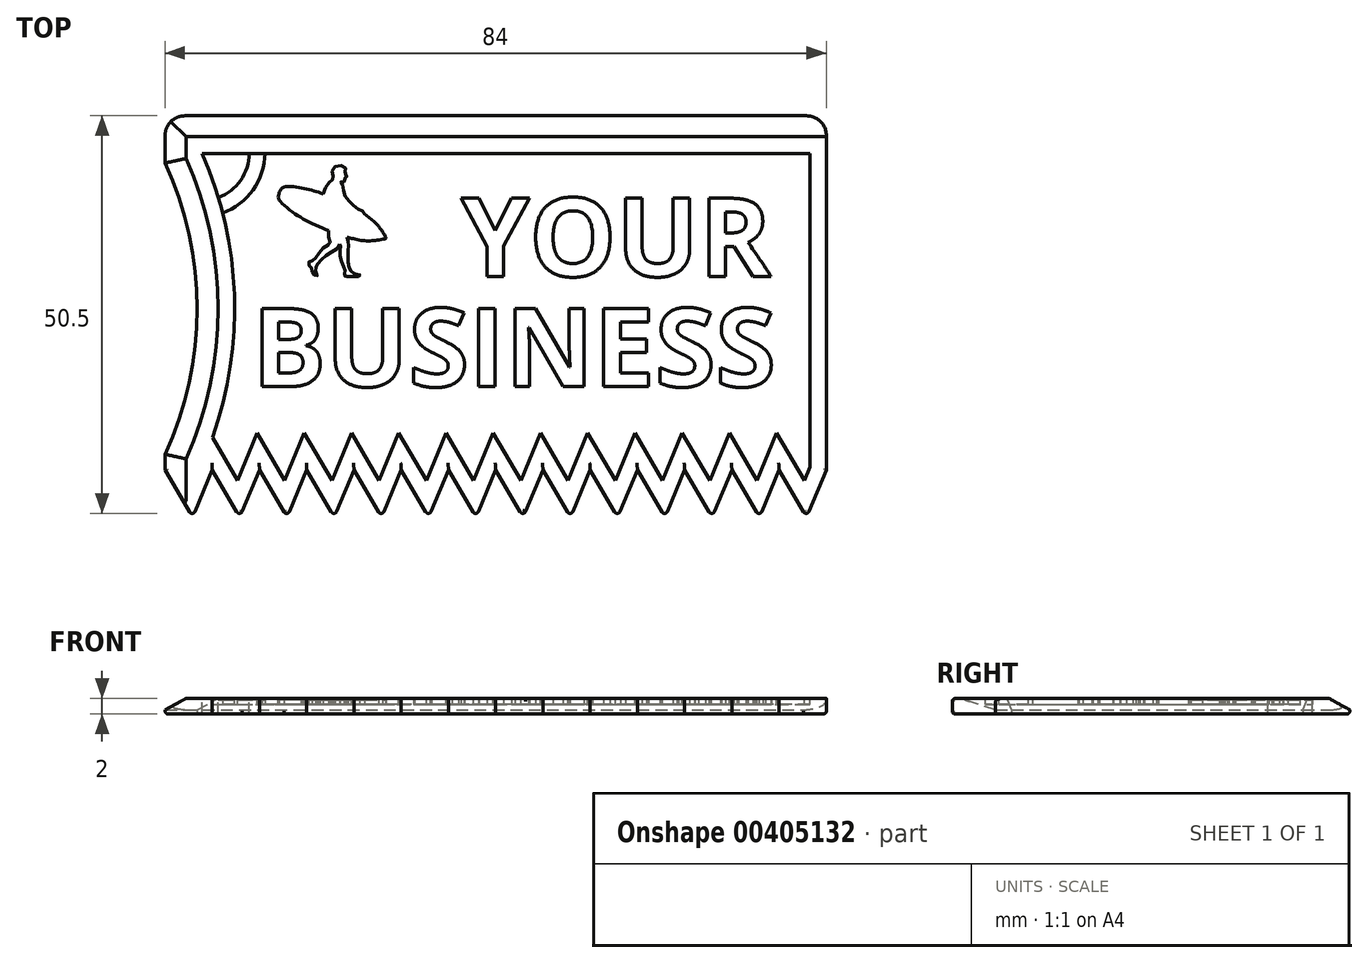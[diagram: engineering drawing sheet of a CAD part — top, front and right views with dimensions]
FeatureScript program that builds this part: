
annotation { "Feature Type Name" : "Feature", "Feature Type Description" : "" }
export const myFeature = defineFeature(function(context is Context, id is Id, definition is map)
    precondition{}
    {
        {
            assignVariable(context, id + "F0", {"name" : "t", "anyValue" : 2});
        }
        {
            var Q0;
            Q0=qCreatedBy(makeId("Top.planeOp"),FACE);
            var sketch = newSketch(context, id + "F1", { "sketchPlane" : qUnion([Q0])});
            skLineSegment(sketch, "E0.bottom", {"start": v(84, 51) * mm, "end": v(0, 51) * mm});
            skLineSegment(sketch, "E0.top", {"start": v(81.5, 0) * mm, "end": v(3.5, 0) * mm, "construction": true});
            skLineSegment(sketch, "E0.left", {"start": v(84, 51) * mm, "end": v(84, 6) * mm});
            skLineSegment(sketch, "E0.right", {"start": v(0, 51) * mm, "end": v(0, 6) * mm, "construction": true});
            skLineSegment(sketch, "E1", {"start": v(84, 6) * mm, "end": v(0, 6) * mm, "construction": true});
            skLineSegment(sketch, "E2", {"start": v(84, 6) * mm, "end": v(81.5, 0) * mm});
            skLineSegment(sketch, "E3", {"start": v(81.5, 0) * mm, "end": v(78, 6) * mm});
            skLineSegment(sketch, "E4.1.0.0", {"start": v(78, 6) * mm, "end": v(75.5, 0) * mm});
            skLineSegment(sketch, "E4.1.0.1", {"start": v(75.5, 0) * mm, "end": v(72, 6) * mm});
            skLineSegment(sketch, "E4.2.0.0", {"start": v(72, 6) * mm, "end": v(69.5, 0) * mm});
            skLineSegment(sketch, "E4.2.0.1", {"start": v(69.5, 0) * mm, "end": v(66, 6) * mm});
            skLineSegment(sketch, "E4.3.0.0", {"start": v(66, 6) * mm, "end": v(63.5, 0) * mm});
            skLineSegment(sketch, "E4.3.0.1", {"start": v(63.5, 0) * mm, "end": v(60, 6) * mm});
            skLineSegment(sketch, "E4.4.0.0", {"start": v(60, 6) * mm, "end": v(57.5, 0) * mm});
            skLineSegment(sketch, "E4.4.0.1", {"start": v(57.5, 0) * mm, "end": v(54, 6) * mm});
            skLineSegment(sketch, "E4.5.0.0", {"start": v(54, 6) * mm, "end": v(51.5, 0) * mm});
            skLineSegment(sketch, "E4.5.0.1", {"start": v(51.5, 0) * mm, "end": v(48, 6) * mm});
            skLineSegment(sketch, "E4.6.0.0", {"start": v(48, 6) * mm, "end": v(45.5, 0) * mm});
            skLineSegment(sketch, "E4.6.0.1", {"start": v(45.5, 0) * mm, "end": v(42, 6) * mm});
            skLineSegment(sketch, "E4.7.0.0", {"start": v(42, 6) * mm, "end": v(39.5, 0) * mm});
            skLineSegment(sketch, "E4.7.0.1", {"start": v(39.5, 0) * mm, "end": v(36, 6) * mm});
            skLineSegment(sketch, "E4.8.0.0", {"start": v(36, 6) * mm, "end": v(33.5, 0) * mm});
            skLineSegment(sketch, "E4.8.0.1", {"start": v(33.5, 0) * mm, "end": v(30, 6) * mm});
            skLineSegment(sketch, "E4.9.0.0", {"start": v(30, 6) * mm, "end": v(27.5, 0) * mm});
            skLineSegment(sketch, "E4.9.0.1", {"start": v(27.5, 0) * mm, "end": v(24, 6) * mm});
            skLineSegment(sketch, "E4.10.0.0", {"start": v(24, 6) * mm, "end": v(21.5, 0) * mm});
            skLineSegment(sketch, "E4.10.0.1", {"start": v(21.5, 0) * mm, "end": v(18, 6) * mm});
            skLineSegment(sketch, "E4.11.0.0", {"start": v(18, 6) * mm, "end": v(15.5, 0) * mm});
            skLineSegment(sketch, "E4.11.0.1", {"start": v(15.5, 0) * mm, "end": v(12, 6) * mm});
            skLineSegment(sketch, "E4.12.0.0", {"start": v(12, 6) * mm, "end": v(9.5, 0) * mm});
            skLineSegment(sketch, "E4.12.0.1", {"start": v(9.5, 0) * mm, "end": v(6, 6) * mm});
            skLineSegment(sketch, "E4.13.0.0", {"start": v(6, 6) * mm, "end": v(3.5, 0) * mm});
            skLineSegment(sketch, "E4.13.0.1", {"start": v(3.5, 0) * mm, "end": v(0, 6) * mm});
            skLineSegment(sketch, "E4.direction1", {"start": v(84, 6) * mm, "end": v(78, 6) * mm, "construction": true});
            skLineSegment(sketch, "E5", {"start": v(0, 6) * mm, "end": v(0, 8) * mm});
            skArc(sketch, "E6", {"start": v(0, 8) * mm, "mid": v(4.07, 26.5) * mm, "end": v(0, 45) * mm});
            skLineSegment(sketch, "E7", {"start": v(0, 45) * mm, "end": v(0, 51) * mm});
            skLineSegment(sketch, "E8", {"start": v(0, 6) * mm, "end": v(0, 0) * mm, "construction": true});
            skSolve(sketch);
        }
        {
            var Q0;
            Q0=qSketchRegion(id+"F1",true);
            extrude(context, id + "F2", {"entities" : qUnion([Q0]), "depth" : (getVariable(context, 't')) * mm});
        }
        {
            var Q0;
            Q0=makeQuery(id+"F2.opExtrude","CAP_EDGE",EDGE,{"disambiguationData":[OSD([sQuery(id+"F1.wireOp",EDGE,"E5")])],"isStart":false});
            var Q1;
            Q1=makeQuery(id+"F2.opExtrude","CAP_EDGE",EDGE,{"disambiguationData":[OSD([sQuery(id+"F1.wireOp",EDGE,"E6")])],"isStart":false});
            var Q2;
            Q2=makeQuery(id+"F2.opExtrude","CAP_EDGE",EDGE,{"disambiguationData":[OSD([sQuery(id+"F1.wireOp",EDGE,"E0.bottom")])],"isStart":false});
            var Q3;
            Q3=makeQuery(id+"F2.opExtrude","CAP_EDGE",EDGE,{"disambiguationData":[OSD([sQuery(id+"F1.wireOp",EDGE,"E7")])],"isStart":false});
            chamfer(context, id + "F3", {"entities" : qUnion([Q0, Q1, Q2, Q3]), "chamferType" : ChamferType.TWO_OFFSETS, "width1" : (getVariable(context, 't') * 2.2 / 3) * mm, "oppositeDirection" : false, "width2" : (getVariable(context, 't') * 4 / 3) * mm, "tangentPropagation" : true});
        }
        {
            var Q0;
            Q0=makeQuery(id+"F2.opExtrude","SWEPT_EDGE",EDGE,{"disambiguationData":[OSD([sQuery(id+"F1.wireOp",EDGE,"E0.bottom"),sQuery(id+"F1.wireOp",EDGE,"E7")])]});
            var Q1;
            Q1=makeQuery(id+"F2.opExtrude","SWEPT_EDGE",EDGE,{"disambiguationData":[OSD([sQuery(id+"F1.wireOp",EDGE,"E0.bottom"),sQuery(id+"F1.wireOp",EDGE,"E0.left")])]});
            fillet(context, id + "F4", {"entities" : qUnion([Q0, Q1]), "radius" : 2.5 * mm, "tangentPropagation" : true, "allowEdgeOverflow" : false});
        }
        {
            var Q0;
            Q0=makeQuery(id+"F2.opExtrude","CAP_FACE",FACE,{"disambiguationData":[OSD([sQuery(id+"F1.wireOp",EDGE,"E0.bottom"),sQuery(id+"F1.wireOp",EDGE,"E0.left"),sQuery(id+"F1.wireOp",EDGE,"E2"),sQuery(id+"F1.wireOp",EDGE,"E3"),sQuery(id+"F1.wireOp",EDGE,"E4.1.0.0"),sQuery(id+"F1.wireOp",EDGE,"E4.1.0.1"),sQuery(id+"F1.wireOp",EDGE,"E4.2.0.0"),sQuery(id+"F1.wireOp",EDGE,"E4.2.0.1"),sQuery(id+"F1.wireOp",EDGE,"E4.3.0.0"),sQuery(id+"F1.wireOp",EDGE,"E4.3.0.1"),sQuery(id+"F1.wireOp",EDGE,"E4.4.0.0"),sQuery(id+"F1.wireOp",EDGE,"E4.4.0.1"),sQuery(id+"F1.wireOp",EDGE,"E4.5.0.0"),sQuery(id+"F1.wireOp",EDGE,"E4.5.0.1"),sQuery(id+"F1.wireOp",EDGE,"E4.6.0.0"),sQuery(id+"F1.wireOp",EDGE,"E4.6.0.1"),sQuery(id+"F1.wireOp",EDGE,"E4.7.0.0"),sQuery(id+"F1.wireOp",EDGE,"E4.7.0.1"),sQuery(id+"F1.wireOp",EDGE,"E4.8.0.0"),sQuery(id+"F1.wireOp",EDGE,"E4.8.0.1"),sQuery(id+"F1.wireOp",EDGE,"E4.9.0.0"),sQuery(id+"F1.wireOp",EDGE,"E4.9.0.1"),sQuery(id+"F1.wireOp",EDGE,"E4.10.0.0"),sQuery(id+"F1.wireOp",EDGE,"E4.10.0.1"),sQuery(id+"F1.wireOp",EDGE,"E4.11.0.0"),sQuery(id+"F1.wireOp",EDGE,"E4.11.0.1"),sQuery(id+"F1.wireOp",EDGE,"E4.12.0.0"),sQuery(id+"F1.wireOp",EDGE,"E4.12.0.1"),sQuery(id+"F1.wireOp",EDGE,"E4.13.0.0"),sQuery(id+"F1.wireOp",EDGE,"E4.13.0.1"),sQuery(id+"F1.wireOp",EDGE,"E5"),sQuery(id+"F1.wireOp",EDGE,"E6"),sQuery(id+"F1.wireOp",EDGE,"E7")])],"isStart":false});
            var sketch = newSketch(context, id + "F5", { "sketchPlane" : qUnion([Q0])});
            skLineSegment(sketch, "E9.0", {"start": v(81.9, 6.42) * mm, "end": v(81.9, 46.23) * mm});
            skLineSegment(sketch, "E9.1", {"start": v(81.19, 4.7) * mm, "end": v(81.9, 6.42) * mm});
            skLineSegment(sketch, "E9.2", {"start": v(77.69, 10.7) * mm, "end": v(81.19, 4.7) * mm});
            skLineSegment(sketch, "E9.3", {"start": v(75.19, 4.7) * mm, "end": v(77.69, 10.7) * mm});
            skLineSegment(sketch, "E9.4", {"start": v(71.69, 10.7) * mm, "end": v(75.19, 4.7) * mm});
            skLineSegment(sketch, "E9.5", {"start": v(69.19, 4.7) * mm, "end": v(71.69, 10.7) * mm});
            skLineSegment(sketch, "E9.6", {"start": v(65.69, 10.7) * mm, "end": v(69.19, 4.7) * mm});
            skLineSegment(sketch, "E9.7", {"start": v(81.9, 46.23) * mm, "end": v(4.67, 46.23) * mm});
            skArc(sketch, "E9.8", {"start": v(4.67, 46.23) * mm, "mid": v(8.8, 28.32) * mm, "end": v(6.02, 10.14) * mm});
            skLineSegment(sketch, "E9.9", {"start": v(6.02, 10.14) * mm, "end": v(9.19, 4.7) * mm});
            skLineSegment(sketch, "E9.10", {"start": v(9.19, 4.7) * mm, "end": v(11.69, 10.7) * mm});
            skLineSegment(sketch, "E9.11", {"start": v(11.69, 10.7) * mm, "end": v(15.19, 4.7) * mm});
            skLineSegment(sketch, "E9.12", {"start": v(15.19, 4.7) * mm, "end": v(17.69, 10.7) * mm});
            skLineSegment(sketch, "E9.13", {"start": v(17.69, 10.7) * mm, "end": v(21.19, 4.7) * mm});
            skLineSegment(sketch, "E9.14", {"start": v(21.19, 4.7) * mm, "end": v(23.69, 10.7) * mm});
            skLineSegment(sketch, "E9.15", {"start": v(23.69, 10.7) * mm, "end": v(27.19, 4.7) * mm});
            skLineSegment(sketch, "E9.16", {"start": v(27.19, 4.7) * mm, "end": v(29.69, 10.7) * mm});
            skLineSegment(sketch, "E9.17", {"start": v(29.69, 10.7) * mm, "end": v(33.19, 4.7) * mm});
            skLineSegment(sketch, "E9.18", {"start": v(33.19, 4.7) * mm, "end": v(35.69, 10.7) * mm});
            skLineSegment(sketch, "E9.19", {"start": v(35.69, 10.7) * mm, "end": v(39.19, 4.7) * mm});
            skLineSegment(sketch, "E9.20", {"start": v(39.19, 4.7) * mm, "end": v(41.69, 10.7) * mm});
            skLineSegment(sketch, "E9.21", {"start": v(41.69, 10.7) * mm, "end": v(45.19, 4.7) * mm});
            skLineSegment(sketch, "E9.22", {"start": v(45.19, 4.7) * mm, "end": v(47.69, 10.7) * mm});
            skLineSegment(sketch, "E9.23", {"start": v(47.69, 10.7) * mm, "end": v(51.19, 4.7) * mm});
            skLineSegment(sketch, "E9.24", {"start": v(51.19, 4.7) * mm, "end": v(53.69, 10.7) * mm});
            skLineSegment(sketch, "E9.25", {"start": v(53.69, 10.7) * mm, "end": v(57.19, 4.7) * mm});
            skLineSegment(sketch, "E9.26", {"start": v(57.19, 4.7) * mm, "end": v(59.69, 10.7) * mm});
            skLineSegment(sketch, "E9.27", {"start": v(59.69, 10.7) * mm, "end": v(63.19, 4.7) * mm});
            skLineSegment(sketch, "E9.28", {"start": v(63.19, 4.7) * mm, "end": v(65.69, 10.7) * mm});
            skSolve(sketch);
        }
        {
            var Q0;
            Q0=makeQuery(id+"F5.imprint","IMPRINT",FACE,{"disambiguationData":[TD([[makeQuery(id+"F5.imprint","IMPRINT",EDGE,{"derivedFrom":sQuery(id+"F5.wireOp",EDGE,"E9.0")}),1.0]])]});
            extrude(context, id + "F6", {"entities" : qUnion([Q0]), "operationType" : NewBodyOperationType.REMOVE, "oppositeDirection" : true, "depth" : (getVariable(context, 't') * 2 / 5) * mm});
        }
        {
            var Q0;
            Q0=makeQuery(id+"F2.opExtrude","CAP_FACE",FACE,{"disambiguationData":[OSD([sQuery(id+"F1.wireOp",EDGE,"E0.bottom"),sQuery(id+"F1.wireOp",EDGE,"E0.left"),sQuery(id+"F1.wireOp",EDGE,"E2"),sQuery(id+"F1.wireOp",EDGE,"E3"),sQuery(id+"F1.wireOp",EDGE,"E4.1.0.0"),sQuery(id+"F1.wireOp",EDGE,"E4.1.0.1"),sQuery(id+"F1.wireOp",EDGE,"E4.2.0.0"),sQuery(id+"F1.wireOp",EDGE,"E4.2.0.1"),sQuery(id+"F1.wireOp",EDGE,"E4.3.0.0"),sQuery(id+"F1.wireOp",EDGE,"E4.3.0.1"),sQuery(id+"F1.wireOp",EDGE,"E4.4.0.0"),sQuery(id+"F1.wireOp",EDGE,"E4.4.0.1"),sQuery(id+"F1.wireOp",EDGE,"E4.5.0.0"),sQuery(id+"F1.wireOp",EDGE,"E4.5.0.1"),sQuery(id+"F1.wireOp",EDGE,"E4.6.0.0"),sQuery(id+"F1.wireOp",EDGE,"E4.6.0.1"),sQuery(id+"F1.wireOp",EDGE,"E4.7.0.0"),sQuery(id+"F1.wireOp",EDGE,"E4.7.0.1"),sQuery(id+"F1.wireOp",EDGE,"E4.8.0.0"),sQuery(id+"F1.wireOp",EDGE,"E4.8.0.1"),sQuery(id+"F1.wireOp",EDGE,"E4.9.0.0"),sQuery(id+"F1.wireOp",EDGE,"E4.9.0.1"),sQuery(id+"F1.wireOp",EDGE,"E4.10.0.0"),sQuery(id+"F1.wireOp",EDGE,"E4.10.0.1"),sQuery(id+"F1.wireOp",EDGE,"E4.11.0.0"),sQuery(id+"F1.wireOp",EDGE,"E4.11.0.1"),sQuery(id+"F1.wireOp",EDGE,"E4.12.0.0"),sQuery(id+"F1.wireOp",EDGE,"E4.12.0.1"),sQuery(id+"F1.wireOp",EDGE,"E4.13.0.0"),sQuery(id+"F1.wireOp",EDGE,"E4.13.0.1"),sQuery(id+"F1.wireOp",EDGE,"E5"),sQuery(id+"F1.wireOp",EDGE,"E6"),sQuery(id+"F1.wireOp",EDGE,"E7")])],"isStart":true});
            var Q1;
            Q1=makeQuery(id+"F2.opExtrude","CAP_EDGE",EDGE,{"disambiguationData":[OSD([sQuery(id+"F1.wireOp",EDGE,"E4.13.0.1")])],"isStart":false});
            var Q2;
            Q2=makeQuery(id+"F2.opExtrude","CAP_EDGE",EDGE,{"disambiguationData":[OSD([sQuery(id+"F1.wireOp",EDGE,"E4.13.0.0")])],"isStart":false});
            var Q3;
            Q3=makeQuery(id+"F2.opExtrude","SWEPT_EDGE",EDGE,{"disambiguationData":[OSD([sQuery(id+"F1.wireOp",EDGE,"E4.13.0.0"),sQuery(id+"F1.wireOp",EDGE,"E4.13.0.1")])]});
            var Q4;
            Q4=makeQuery(id+"F2.opExtrude","CAP_EDGE",EDGE,{"disambiguationData":[OSD([sQuery(id+"F1.wireOp",EDGE,"E4.12.0.1")])],"isStart":false});
            var Q5;
            Q5=makeQuery(id+"F2.opExtrude","SWEPT_EDGE",EDGE,{"disambiguationData":[OSD([sQuery(id+"F1.wireOp",EDGE,"E4.12.0.0"),sQuery(id+"F1.wireOp",EDGE,"E4.12.0.1")])]});
            var Q6;
            Q6=makeQuery(id+"F2.opExtrude","CAP_EDGE",EDGE,{"disambiguationData":[OSD([sQuery(id+"F1.wireOp",EDGE,"E4.12.0.0")])],"isStart":false});
            var Q7;
            Q7=makeQuery(id+"F2.opExtrude","CAP_EDGE",EDGE,{"disambiguationData":[OSD([sQuery(id+"F1.wireOp",EDGE,"E4.11.0.1")])],"isStart":false});
            var Q8;
            Q8=makeQuery(id+"F2.opExtrude","SWEPT_EDGE",EDGE,{"disambiguationData":[OSD([sQuery(id+"F1.wireOp",EDGE,"E4.11.0.0"),sQuery(id+"F1.wireOp",EDGE,"E4.11.0.1")])]});
            var Q9;
            Q9=makeQuery(id+"F2.opExtrude","CAP_EDGE",EDGE,{"disambiguationData":[OSD([sQuery(id+"F1.wireOp",EDGE,"E4.11.0.0")])],"isStart":false});
            var Q10;
            Q10=makeQuery(id+"F2.opExtrude","CAP_EDGE",EDGE,{"disambiguationData":[OSD([sQuery(id+"F1.wireOp",EDGE,"E4.10.0.1")])],"isStart":false});
            var Q11;
            Q11=makeQuery(id+"F2.opExtrude","CAP_EDGE",EDGE,{"disambiguationData":[OSD([sQuery(id+"F1.wireOp",EDGE,"E4.10.0.0")])],"isStart":false});
            var Q12;
            Q12=makeQuery(id+"F2.opExtrude","CAP_EDGE",EDGE,{"disambiguationData":[OSD([sQuery(id+"F1.wireOp",EDGE,"E4.9.0.1")])],"isStart":false});
            var Q13;
            Q13=makeQuery(id+"F2.opExtrude","CAP_EDGE",EDGE,{"disambiguationData":[OSD([sQuery(id+"F1.wireOp",EDGE,"E4.9.0.0")])],"isStart":false});
            var Q14;
            Q14=makeQuery(id+"F2.opExtrude","CAP_EDGE",EDGE,{"disambiguationData":[OSD([sQuery(id+"F1.wireOp",EDGE,"E4.8.0.1")])],"isStart":false});
            var Q15;
            Q15=makeQuery(id+"F2.opExtrude","CAP_EDGE",EDGE,{"disambiguationData":[OSD([sQuery(id+"F1.wireOp",EDGE,"E4.8.0.0")])],"isStart":false});
            var Q16;
            Q16=makeQuery(id+"F2.opExtrude","CAP_EDGE",EDGE,{"disambiguationData":[OSD([sQuery(id+"F1.wireOp",EDGE,"E4.7.0.1")])],"isStart":false});
            var Q17;
            Q17=makeQuery(id+"F2.opExtrude","CAP_EDGE",EDGE,{"disambiguationData":[OSD([sQuery(id+"F1.wireOp",EDGE,"E4.7.0.0")])],"isStart":false});
            var Q18;
            Q18=makeQuery(id+"F2.opExtrude","CAP_EDGE",EDGE,{"disambiguationData":[OSD([sQuery(id+"F1.wireOp",EDGE,"E4.6.0.1")])],"isStart":false});
            var Q19;
            Q19=makeQuery(id+"F2.opExtrude","CAP_EDGE",EDGE,{"disambiguationData":[OSD([sQuery(id+"F1.wireOp",EDGE,"E4.6.0.0")])],"isStart":false});
            var Q20;
            Q20=makeQuery(id+"F2.opExtrude","CAP_EDGE",EDGE,{"disambiguationData":[OSD([sQuery(id+"F1.wireOp",EDGE,"E4.5.0.1")])],"isStart":false});
            var Q21;
            Q21=makeQuery(id+"F2.opExtrude","CAP_EDGE",EDGE,{"disambiguationData":[OSD([sQuery(id+"F1.wireOp",EDGE,"E4.5.0.0")])],"isStart":false});
            var Q22;
            Q22=makeQuery(id+"F2.opExtrude","CAP_EDGE",EDGE,{"disambiguationData":[OSD([sQuery(id+"F1.wireOp",EDGE,"E4.4.0.1")])],"isStart":false});
            var Q23;
            Q23=makeQuery(id+"F2.opExtrude","CAP_EDGE",EDGE,{"disambiguationData":[OSD([sQuery(id+"F1.wireOp",EDGE,"E4.4.0.0")])],"isStart":false});
            var Q24;
            Q24=makeQuery(id+"F2.opExtrude","CAP_EDGE",EDGE,{"disambiguationData":[OSD([sQuery(id+"F1.wireOp",EDGE,"E4.3.0.1")])],"isStart":false});
            var Q25;
            Q25=makeQuery(id+"F2.opExtrude","CAP_EDGE",EDGE,{"disambiguationData":[OSD([sQuery(id+"F1.wireOp",EDGE,"E4.3.0.0")])],"isStart":false});
            var Q26;
            Q26=makeQuery(id+"F2.opExtrude","CAP_EDGE",EDGE,{"disambiguationData":[OSD([sQuery(id+"F1.wireOp",EDGE,"E4.2.0.1")])],"isStart":false});
            var Q27;
            Q27=makeQuery(id+"F2.opExtrude","CAP_EDGE",EDGE,{"disambiguationData":[OSD([sQuery(id+"F1.wireOp",EDGE,"E4.2.0.0")])],"isStart":false});
            var Q28;
            Q28=makeQuery(id+"F2.opExtrude","CAP_EDGE",EDGE,{"disambiguationData":[OSD([sQuery(id+"F1.wireOp",EDGE,"E4.1.0.1")])],"isStart":false});
            var Q29;
            Q29=makeQuery(id+"F2.opExtrude","CAP_EDGE",EDGE,{"disambiguationData":[OSD([sQuery(id+"F1.wireOp",EDGE,"E4.1.0.0")])],"isStart":false});
            var Q30;
            Q30=makeQuery(id+"F2.opExtrude","CAP_EDGE",EDGE,{"disambiguationData":[OSD([sQuery(id+"F1.wireOp",EDGE,"E3")])],"isStart":false});
            var Q31;
            Q31=makeQuery(id+"F2.opExtrude","SWEPT_EDGE",EDGE,{"disambiguationData":[OSD([sQuery(id+"F1.wireOp",EDGE,"E2"),sQuery(id+"F1.wireOp",EDGE,"E3")])]});
            var Q32;
            Q32=makeQuery(id+"F2.opExtrude","CAP_EDGE",EDGE,{"disambiguationData":[OSD([sQuery(id+"F1.wireOp",EDGE,"E2")])],"isStart":false});
            var Q33;
            Q33=makeQuery(id+"F2.opExtrude","SWEPT_EDGE",EDGE,{"disambiguationData":[OSD([sQuery(id+"F1.wireOp",EDGE,"E4.1.0.0"),sQuery(id+"F1.wireOp",EDGE,"E4.1.0.1")])]});
            var Q34;
            Q34=makeQuery(id+"F2.opExtrude","SWEPT_EDGE",EDGE,{"disambiguationData":[OSD([sQuery(id+"F1.wireOp",EDGE,"E4.2.0.0"),sQuery(id+"F1.wireOp",EDGE,"E4.2.0.1")])]});
            var Q35;
            Q35=makeQuery(id+"F2.opExtrude","SWEPT_EDGE",EDGE,{"disambiguationData":[OSD([sQuery(id+"F1.wireOp",EDGE,"E4.3.0.0"),sQuery(id+"F1.wireOp",EDGE,"E4.3.0.1")])]});
            var Q36;
            Q36=makeQuery(id+"F2.opExtrude","SWEPT_EDGE",EDGE,{"disambiguationData":[OSD([sQuery(id+"F1.wireOp",EDGE,"E4.4.0.0"),sQuery(id+"F1.wireOp",EDGE,"E4.4.0.1")])]});
            var Q37;
            Q37=makeQuery(id+"F2.opExtrude","SWEPT_EDGE",EDGE,{"disambiguationData":[OSD([sQuery(id+"F1.wireOp",EDGE,"E4.5.0.0"),sQuery(id+"F1.wireOp",EDGE,"E4.5.0.1")])]});
            var Q38;
            Q38=makeQuery(id+"F2.opExtrude","SWEPT_EDGE",EDGE,{"disambiguationData":[OSD([sQuery(id+"F1.wireOp",EDGE,"E4.6.0.0"),sQuery(id+"F1.wireOp",EDGE,"E4.6.0.1")])]});
            var Q39;
            Q39=makeQuery(id+"F2.opExtrude","SWEPT_EDGE",EDGE,{"disambiguationData":[OSD([sQuery(id+"F1.wireOp",EDGE,"E4.7.0.0"),sQuery(id+"F1.wireOp",EDGE,"E4.7.0.1")])]});
            var Q40;
            Q40=makeQuery(id+"F2.opExtrude","SWEPT_EDGE",EDGE,{"disambiguationData":[OSD([sQuery(id+"F1.wireOp",EDGE,"E4.8.0.0"),sQuery(id+"F1.wireOp",EDGE,"E4.8.0.1")])]});
            var Q41;
            Q41=makeQuery(id+"F2.opExtrude","SWEPT_EDGE",EDGE,{"disambiguationData":[OSD([sQuery(id+"F1.wireOp",EDGE,"E4.9.0.0"),sQuery(id+"F1.wireOp",EDGE,"E4.9.0.1")])]});
            var Q42;
            Q42=makeQuery(id+"F2.opExtrude","SWEPT_EDGE",EDGE,{"disambiguationData":[OSD([sQuery(id+"F1.wireOp",EDGE,"E4.10.0.0"),sQuery(id+"F1.wireOp",EDGE,"E4.10.0.1")])]});
            fillet(context, id + "F7", {"entities" : qUnion([Q0, Q1, Q2, Q3, Q4, Q5, Q6, Q7, Q8, Q9, Q10, Q11, Q12, Q13, Q14, Q15, Q16, Q17, Q18, Q19, Q20, Q21, Q22, Q23, Q24, Q25, Q26, Q27, Q28, Q29, Q30, Q31, Q32, Q33, Q34, Q35, Q36, Q37, Q38, Q39, Q40, Q41, Q42]), "radius" : .4 * mm, "tangentPropagation" : true, "allowEdgeOverflow" : false});
        }
        {
            var Q0;
            Q0=makeQuery(id+"F6.boolean.opBoolean","COPY",FACE,{"derivedFrom":makeQuery(id+"F6.opExtrude","CAP_FACE",FACE,{"disambiguationData":[OSD([sQuery(id+"F5.wireOp",EDGE,"E9.0"),sQuery(id+"F5.wireOp",EDGE,"E9.1"),sQuery(id+"F5.wireOp",EDGE,"E9.2"),sQuery(id+"F5.wireOp",EDGE,"E9.3"),sQuery(id+"F5.wireOp",EDGE,"E9.4"),sQuery(id+"F5.wireOp",EDGE,"E9.5"),sQuery(id+"F5.wireOp",EDGE,"E9.6"),sQuery(id+"F5.wireOp",EDGE,"E9.7"),sQuery(id+"F5.wireOp",EDGE,"E9.8"),sQuery(id+"F5.wireOp",EDGE,"E9.9"),sQuery(id+"F5.wireOp",EDGE,"E9.10"),sQuery(id+"F5.wireOp",EDGE,"E9.11"),sQuery(id+"F5.wireOp",EDGE,"E9.12"),sQuery(id+"F5.wireOp",EDGE,"E9.13"),sQuery(id+"F5.wireOp",EDGE,"E9.14"),sQuery(id+"F5.wireOp",EDGE,"E9.15"),sQuery(id+"F5.wireOp",EDGE,"E9.16"),sQuery(id+"F5.wireOp",EDGE,"E9.17"),sQuery(id+"F5.wireOp",EDGE,"E9.18"),sQuery(id+"F5.wireOp",EDGE,"E9.19"),sQuery(id+"F5.wireOp",EDGE,"E9.20"),sQuery(id+"F5.wireOp",EDGE,"E9.21"),sQuery(id+"F5.wireOp",EDGE,"E9.22"),sQuery(id+"F5.wireOp",EDGE,"E9.23"),sQuery(id+"F5.wireOp",EDGE,"E9.24"),sQuery(id+"F5.wireOp",EDGE,"E9.25"),sQuery(id+"F5.wireOp",EDGE,"E9.26"),sQuery(id+"F5.wireOp",EDGE,"E9.27"),sQuery(id+"F5.wireOp",EDGE,"E9.28")])],"isStart":false})});
            var sketch = newSketch(context, id + "F8", { "sketchPlane" : qUnion([Q0])});
            skText(sketch, "E10", { "text": "BUSINESS", "fontName": "OpenSans-Bold.ttf"});
            skText(sketch, "E11", { "text": "YOUR", "fontName": "OpenSans-Bold.ttf"});
            const initialGuessF8  = {"E10": [0.0111, 0.01661, 1, 0, 0.01], "E11": [0.0376, 0.03061, 1, 0, 0.01]};
            skSetInitialGuess(sketch, initialGuessF8);
            skSolve(sketch);
        }
        {
            var Q0;
            Q0=makeQuery(id+"F8.imprint","IMPRINT",FACE,{"disambiguationData":[TD([[makeQuery(id+"F8.imprint","IMPRINT",EDGE,{"derivedFrom":sQuery(id+"F8.wireOp",EDGE,"E10.sketch_text.stroke-0")}),1.0]])]});
            var sketch = newSketch(context, id + "F9", { "sketchPlane" : qUnion([Q0])});
            skLineSegment(sketch, "E12.0", {"start": v(81.9, 46.23) * mm, "end": v(4.67, 46.23) * mm});
            skArc(sketch, "E12.1", {"start": v(4.67, 46.23) * mm, "mid": v(8.8, 28.32) * mm, "end": v(6.02, 10.14) * mm});
            skPoint(sketch, "E12.2", {"position": v(4.67, 46.23) * mm});
            skArc(sketch, "E13", {"start": v(6.76, 40.6) * mm, "mid": v(9.6, 42.8) * mm, "end": v(10.67, 46.23) * mm});
            skArc(sketch, "E14", {"start": v(7.3, 38.68) * mm, "mid": v(11.2, 41.6) * mm, "end": v(12.67, 46.23) * mm});
            skLineSegment(sketch, "E15", {"start": v(14.33, 41.37) * mm, "end": v(28.35, 35.34) * mm, "construction": true});
            skFitSpline(sketch, "E16", {"points": [v(20.78, 36.4) * mm, v(18.17, 37.57) * mm, v(16.2, 38.77) * mm, v(14.57, 40.2) * mm, v(14.39, 40.75) * mm, v(14.51, 41.3) * mm], "startDerivative": vector(-8.18, 3.62) * mm, "endDerivative": vector(1.44, 4.42) * mm});
            skFitSpline(sketch, "E17", {"points": [v(21.8, 40.38) * mm, v(19.73, 41.2) * mm, v(17.5, 41.8) * mm, v(15.34, 42) * mm, v(14.82, 41.76) * mm, v(14.51, 41.3) * mm], "startDerivative": vector(-8.26, 3.44) * mm, "endDerivative": vector(-2.21, -4.08) * mm});
            skFitSpline(sketch, "E18", {"points": [v(20.78, 36.4) * mm, v(20.78, 35.64) * mm, v(20.95, 35.07) * mm, v(20.96, 34.8) * mm, v(20.8, 34.66) * mm, v(20.25, 34.4) * mm, v(19.79, 33.88) * mm, v(19.35, 33.26) * mm, v(19, 32.82) * mm, v(18.79, 32.65) * mm, v(18.48, 32.52) * mm, v(18.27, 32.44) * mm, v(18.2, 32.27) * mm, v(18.32, 31.93) * mm, v(18.48, 31.77) * mm, v(18.61, 31.65) * mm, v(18.65, 31.45) * mm, v(18.68, 31.05) * mm, v(18.84, 30.85) * mm, v(19.05, 30.74) * mm, v(19.33, 30.68) * mm, v(19.38, 30.7) * mm, v(19.39, 30.75) * mm, v(19.36, 30.83) * mm, v(19.24, 30.92) * mm, v(19.13, 31.03) * mm, v(19.11, 31.31) * mm, v(19.14, 31.62) * mm, v(19.17, 31.85) * mm, v(19.25, 32.01) * mm, v(19.45, 32.31) * mm, v(19.98, 32.83) * mm, v(20.57, 33.32) * mm, v(21.18, 33.76) * mm, v(21.73, 34.08) * mm, v(21.96, 34.28) * mm, v(22.05, 34.5) * mm, v(22.1, 34.7) * mm, v(22.15, 34.73) * mm, v(22.18, 34.73) * mm], "startDerivative": vector(-1.7, -19.21) * mm, "endDerivative": vector(3.01, -1.59) * mm});
            skFitSpline(sketch, "E19", {"points": [v(20.05, 41.08) * mm, v(20.31, 41.73) * mm, v(20.57, 42.25) * mm, v(20.85, 42.54) * mm, v(21.15, 42.79) * mm, v(21.36, 42.97) * mm, v(21.42, 43.1) * mm, v(21.3, 43.35) * mm, v(21.2, 43.69) * mm, v(21.26, 44.09) * mm, v(21.42, 44.41) * mm, v(21.96, 44.72) * mm, v(22.41, 44.65) * mm, v(22.73, 44.52) * mm, v(22.95, 44.3) * mm, v(22.93, 44.07) * mm, v(22.87, 43.95) * mm, v(22.93, 43.83) * mm, v(22.96, 43.68) * mm, v(22.91, 43.6) * mm, v(22.9, 43.54) * mm, v(22.98, 43.43) * mm, v(23.06, 43.31) * mm, v(23.06, 43.23) * mm, v(23.02, 43.17) * mm, v(22.9, 43.2) * mm, v(22.89, 43.13) * mm, v(22.89, 43.03) * mm, v(22.86, 42.96) * mm, v(22.81, 42.9) * mm, v(22.82, 42.8) * mm, v(22.85, 42.72) * mm, v(22.83, 42.65) * mm, v(22.74, 42.62) * mm, v(22.65, 42.58) * mm, v(22.47, 42.6) * mm, v(22.37, 42.6) * mm, v(22.3, 42.56) * mm, v(22.37, 42.46) * mm, v(22.53, 42.3) * mm, v(22.67, 41.97) * mm, v(22.68, 41.44) * mm, v(22.8, 40.96) * mm, v(23.02, 40.5) * mm, v(23.5, 40.04) * mm, v(23.89, 39.68) * mm, v(24.31, 39.38) * mm, v(24.62, 39.05) * mm, v(24.88, 38.93) * mm, v(25.2, 38.8) * mm, v(25.31, 38.6) * mm, v(25.34, 38.5) * mm], "startDerivative": vector(7.84, 19.36) * mm, "endDerivative": vector(2.4, -8.81) * mm});
            skFitSpline(sketch, "E20", {"points": [v(23.11, 35.6) * mm, v(23.77, 35.42) * mm, v(24.73, 35.21) * mm, v(25.68, 35.1) * mm, v(26.5, 35.15) * mm, v(27.4, 35.27) * mm, v(28.03, 35.44) * mm, v(28.05, 35.47) * mm], "startDerivative": vector(4.26, -1.27) * mm, "endDerivative": vector(0.24, 0.98) * mm});
            skFitSpline(sketch, "E21.MirrorCS", {"points": [v(24.56, 38.97) * mm, v(25.15, 38.62) * mm, v(25.96, 38.06) * mm, v(26.68, 37.45) * mm, v(27.23, 36.82) * mm, v(27.75, 36.09) * mm, v(28.06, 35.52) * mm, v(28.05, 35.47) * mm], "startDerivative": vector(3.85, -2.22) * mm, "endDerivative": vector(-0.55, -0.85) * mm});
            skFitSpline(sketch, "E22", {"points": [v(23.11, 35.6) * mm, v(23.22, 35.14) * mm, v(23.28, 34.82) * mm, v(23.26, 34.39) * mm, v(23.22, 33.76) * mm, v(23.23, 33.07) * mm, v(23.28, 32.27) * mm, v(23.41, 31.6) * mm, v(23.57, 31.3) * mm, v(23.85, 31.1) * mm, v(24.1, 30.94) * mm, v(24.4, 30.87) * mm, v(24.63, 30.85) * mm, v(24.73, 30.83) * mm, v(24.73, 30.75) * mm, v(24.68, 30.67) * mm, v(24.57, 30.62) * mm, v(24.4, 30.58) * mm, v(24.1, 30.57) * mm, v(23.65, 30.57) * mm, v(23.34, 30.59) * mm, v(23.1, 30.58) * mm, v(22.93, 30.59) * mm, v(22.84, 30.63) * mm, v(22.8, 30.76) * mm, v(22.8, 30.93) * mm, v(22.87, 31.1) * mm, v(22.87, 31.29) * mm, v(22.75, 31.62) * mm, v(22.54, 32.2) * mm, v(22.35, 32.86) * mm, v(22.2, 33.51) * mm, v(22.26, 34.1) * mm, v(22.28, 34.5) * mm, v(22.26, 34.67) * mm, v(22.18, 34.73) * mm], "startDerivative": vector(2.94, -13.83) * mm, "endDerivative": vector(-5.6, 2.93) * mm});
            skSolve(sketch);
        }
        {
            var Q0;
            Q0=qSketchRegion(id+"F8",true);
            var Q1;
            Q1=makeQuery(id+"F2.opExtrude","CAP_FACE",FACE,{"disambiguationData":[OSD([sQuery(id+"F1.wireOp",EDGE,"E0.bottom"),sQuery(id+"F1.wireOp",EDGE,"E0.left"),sQuery(id+"F1.wireOp",EDGE,"E2"),sQuery(id+"F1.wireOp",EDGE,"E3"),sQuery(id+"F1.wireOp",EDGE,"E4.1.0.0"),sQuery(id+"F1.wireOp",EDGE,"E4.1.0.1"),sQuery(id+"F1.wireOp",EDGE,"E4.2.0.0"),sQuery(id+"F1.wireOp",EDGE,"E4.2.0.1"),sQuery(id+"F1.wireOp",EDGE,"E4.3.0.0"),sQuery(id+"F1.wireOp",EDGE,"E4.3.0.1"),sQuery(id+"F1.wireOp",EDGE,"E4.4.0.0"),sQuery(id+"F1.wireOp",EDGE,"E4.4.0.1"),sQuery(id+"F1.wireOp",EDGE,"E4.5.0.0"),sQuery(id+"F1.wireOp",EDGE,"E4.5.0.1"),sQuery(id+"F1.wireOp",EDGE,"E4.6.0.0"),sQuery(id+"F1.wireOp",EDGE,"E4.6.0.1"),sQuery(id+"F1.wireOp",EDGE,"E4.7.0.0"),sQuery(id+"F1.wireOp",EDGE,"E4.7.0.1"),sQuery(id+"F1.wireOp",EDGE,"E4.8.0.0"),sQuery(id+"F1.wireOp",EDGE,"E4.8.0.1"),sQuery(id+"F1.wireOp",EDGE,"E4.9.0.0"),sQuery(id+"F1.wireOp",EDGE,"E4.9.0.1"),sQuery(id+"F1.wireOp",EDGE,"E4.10.0.0"),sQuery(id+"F1.wireOp",EDGE,"E4.10.0.1"),sQuery(id+"F1.wireOp",EDGE,"E4.11.0.0"),sQuery(id+"F1.wireOp",EDGE,"E4.11.0.1"),sQuery(id+"F1.wireOp",EDGE,"E4.12.0.0"),sQuery(id+"F1.wireOp",EDGE,"E4.12.0.1"),sQuery(id+"F1.wireOp",EDGE,"E4.13.0.0"),sQuery(id+"F1.wireOp",EDGE,"E4.13.0.1"),sQuery(id+"F1.wireOp",EDGE,"E5"),sQuery(id+"F1.wireOp",EDGE,"E6"),sQuery(id+"F1.wireOp",EDGE,"E7")])],"isStart":false});
            extrude(context, id + "F10", {"entities" : qUnion([Q0]), "operationType" : NewBodyOperationType.ADD, "endBound" : BoundingType.UP_TO_SURFACE, "endBoundEntityFace" : qUnion([Q1]), "depth" : 25 * mm});
        }
        {
            var Q0;
            {var subQ3=sQuery(id+"F9.wireOp",EDGE,"E13");Q0=makeQuery(id+"F9.imprint","IMPRINT",FACE,{"disambiguationData":[TD([[makeQuery(id+"F9.imprint","IMPRINT",EDGE,{"derivedFrom":subQ3}),1.0]])]});}
            extrude(context, id + "F11", {"entities" : qUnion([Q0]), "operationType" : NewBodyOperationType.REMOVE, "oppositeDirection" : true, "depth" : 25 * mm});
        }
        {
            var Q0;
            {var subQ0=sQuery(id+"F9.wireOp",EDGE,"E13");Q0=makeQuery(id+"F9.imprint","IMPRINT",FACE,{"disambiguationData":[TD([[makeQuery(id+"F9.imprint","IMPRINT",EDGE,{"derivedFrom":subQ0}),-1.0]])]});}
            var Q1;
            Q1=makeQuery(id+"F9.imprint","IMPRINT",FACE,{"disambiguationData":[TD([[makeQuery(id+"F9.imprint","IMPRINT",EDGE,{"derivedFrom":sQuery(id+"F9.wireOp",EDGE,"E16")}),-1.0]])]});
            extrude(context, id + "F12", {"entities" : qUnion([Q0, Q1]), "operationType" : NewBodyOperationType.ADD, "depth" : .6 * mm});
        }
    });
